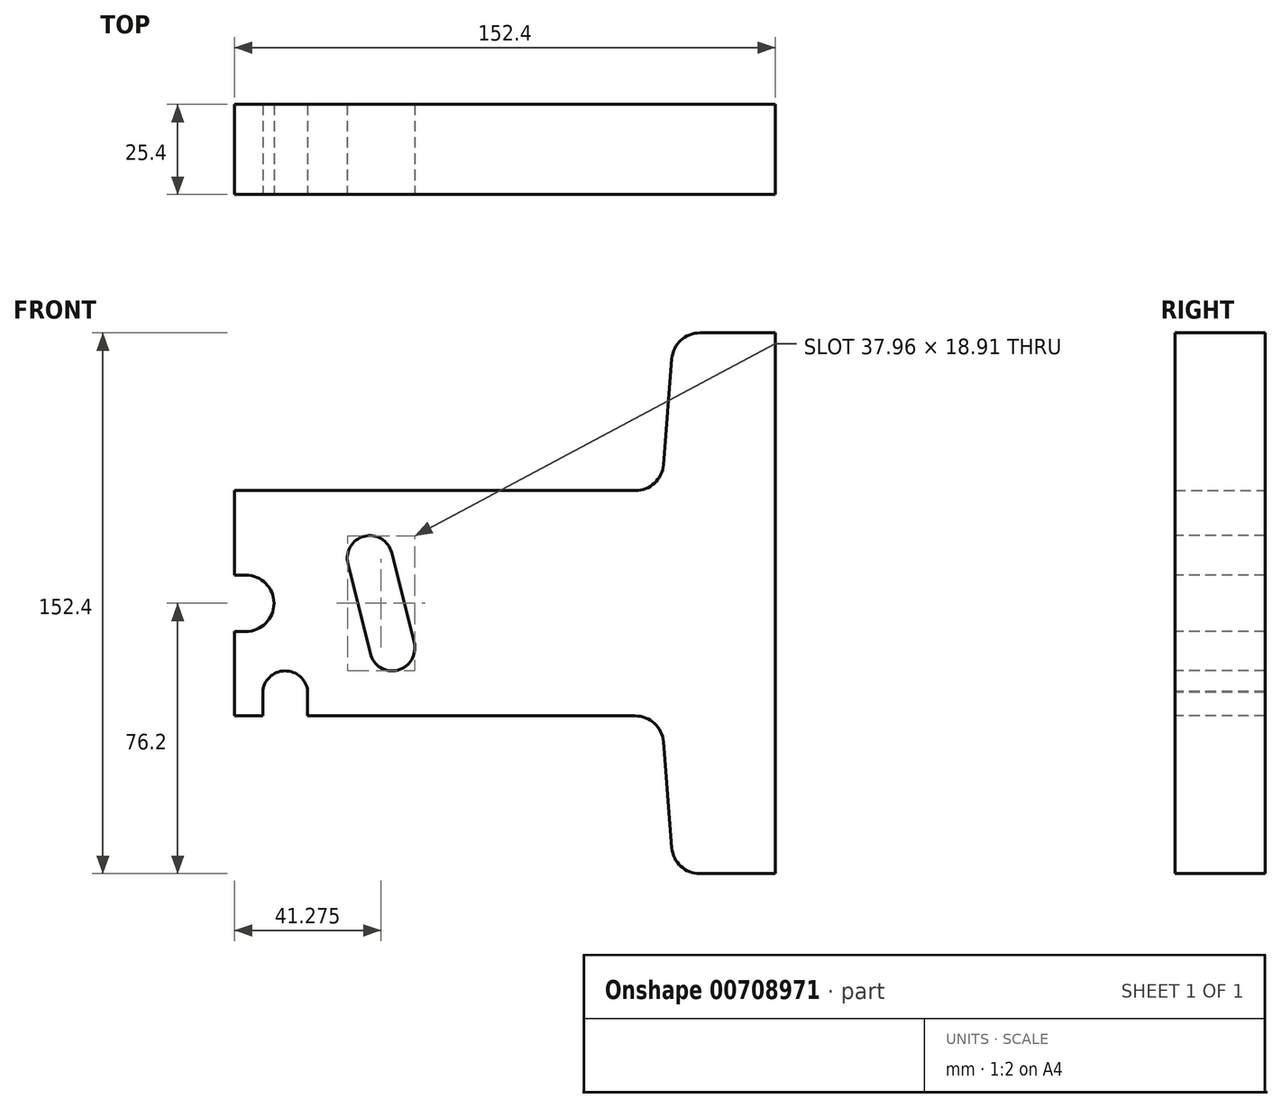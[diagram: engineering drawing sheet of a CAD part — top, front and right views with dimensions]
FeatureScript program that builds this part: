
annotation { "Feature Type Name" : "Feature", "Feature Type Description" : "" }
export const myFeature = defineFeature(function(context is Context, id is Id, definition is map)
    precondition{}
    {
        {
            var Q0;
            Q0=qCreatedBy(makeId("Front.planeOp"),FACE);
            var sketch = newSketch(context, id + "F0", { "sketchPlane" : qUnion([Q0])});
            skLineSegment(sketch, "E0", {"start": v(76.2, 0) * mm, "end": v(76.2, -76.2) * mm});
            skLineSegment(sketch, "E1", {"start": v(76.2, -76.2) * mm, "end": v(54.95, -76.2) * mm});
            skLineSegment(sketch, "E2", {"start": v(-76.2, 0) * mm, "end": v(-76.2, -31.75) * mm});
            skLineSegment(sketch, "E3", {"start": v(-76.2, -31.75) * mm, "end": v(36.73, -31.75) * mm});
            skLineSegment(sketch, "E4", {"start": v(47.04, -68.9) * mm, "end": v(44.65, -39.05) * mm});
            skLineSegment(sketch, "E5.MirrorCS", {"start": v(-76.2, 0) * mm, "end": v(-76.2, 31.75) * mm});
            skLineSegment(sketch, "E6.MirrorCS", {"start": v(-76.2, 31.75) * mm, "end": v(36.73, 31.75) * mm});
            skLineSegment(sketch, "E7.MirrorCS", {"start": v(47.04, 68.9) * mm, "end": v(44.65, 39.05) * mm});
            skLineSegment(sketch, "E8.MirrorCS", {"start": v(76.2, 76.2) * mm, "end": v(54.95, 76.2) * mm});
            skLineSegment(sketch, "E9.MirrorCS", {"start": v(76.2, 0) * mm, "end": v(76.2, 76.2) * mm});
            skPoint(sketch, "E10.visualSharp", {"position": v(44.06, 31.75) * mm});
            skArc(sketch, "E10.filletArc", {"start": v(36.73, 31.75) * mm, "mid": v(42.12, 33.85) * mm, "end": v(44.65, 39.05) * mm});
            skPoint(sketch, "E11.visualSharp", {"position": v(44.06, -31.75) * mm});
            skArc(sketch, "E11.filletArc", {"start": v(44.65, -39.05) * mm, "mid": v(42.12, -33.85) * mm, "end": v(36.73, -31.75) * mm});
            skPoint(sketch, "E12.visualSharp", {"position": v(47.63, 76.2) * mm});
            skArc(sketch, "E12.filletArc", {"start": v(54.95, 76.2) * mm, "mid": v(49.57, 74.1) * mm, "end": v(47.04, 68.9) * mm});
            skPoint(sketch, "E13.visualSharp", {"position": v(47.63, -76.2) * mm});
            skArc(sketch, "E13.filletArc", {"start": v(47.04, -68.9) * mm, "mid": v(49.57, -74.1) * mm, "end": v(54.95, -76.2) * mm});
            skSolve(sketch);
        }
        {
            var Q0;
            Q0=makeQuery(id+"F0.imprint","IMPRINT",FACE,{"disambiguationData":[TD([[makeQuery(id+"F0.imprint","IMPRINT",EDGE,{"derivedFrom":sQuery(id+"F0.wireOp",EDGE,"E0")}),-1.0]])]});
            extrude(context, id + "F1", {"entities" : qUnion([Q0]), "depth" : 25.4 * mm, "offsetDistance" : 25.4 * mm, "symmetric" : true});
        }
        {
            var Q0;
            Q0=makeQuery(id+"F1.opExtrude","CAP_FACE",FACE,{"disambiguationData":[OSD([sQuery(id+"F0.wireOp",EDGE,"E0"),sQuery(id+"F0.wireOp",EDGE,"E1"),sQuery(id+"F0.wireOp",EDGE,"E2"),sQuery(id+"F0.wireOp",EDGE,"E3"),sQuery(id+"F0.wireOp",EDGE,"E4"),sQuery(id+"F0.wireOp",EDGE,"E5.MirrorCS"),sQuery(id+"F0.wireOp",EDGE,"E6.MirrorCS"),sQuery(id+"F0.wireOp",EDGE,"E7.MirrorCS"),sQuery(id+"F0.wireOp",EDGE,"E8.MirrorCS"),sQuery(id+"F0.wireOp",EDGE,"E9.MirrorCS")])],"isStart":false});
            var sketch = newSketch(context, id + "F2", { "sketchPlane" : qUnion([Q0])});
            skLineSegment(sketch, "E14", {"start": v(-73.03, 7.94) * mm, "end": v(-76.2, 7.94) * mm});
            skLineSegment(sketch, "E15", {"start": v(-73.03, -7.94) * mm, "end": v(-76.2, -7.94) * mm});
            skLineSegment(sketch, "E16", {"start": v(-65.09, 0) * mm, "end": v(-65.09, 0) * mm});
            skPoint(sketch, "E17.visualSharp", {"position": v(-65.09, 7.94) * mm});
            skArc(sketch, "E17.filletArc", {"start": v(-65.09, 0) * mm, "mid": v(-67.41, 5.61) * mm, "end": v(-73.03, 7.94) * mm});
            skPoint(sketch, "E18.visualSharp", {"position": v(-65.09, -7.94) * mm});
            skArc(sketch, "E18.filletArc", {"start": v(-73.03, -7.94) * mm, "mid": v(-67.41, -5.61) * mm, "end": v(-65.09, 0) * mm});
            skSolve(sketch);
        }
        {
            var Q0;
            {var subQ0=sQuery(id+"F2.wireOp",EDGE,"E14");Q0=makeQuery(id+"F2.imprint","IMPRINT",FACE,{"disambiguationData":[TD([[makeQuery(id+"F2.imprint","IMPRINT",EDGE,{"derivedFrom":subQ0}),1.0]])]});}
            extrude(context, id + "F3", {"entities" : qUnion([Q0]), "operationType" : NewBodyOperationType.REMOVE, "endBound" : BoundingType.THROUGH_ALL, "oppositeDirection" : true, "depth" : 25.4 * mm, "offsetDistance" : 25.4 * mm});
        }
        {
            var Q0;
            Q0=makeQuery(id+"F1.opExtrude","CAP_FACE",FACE,{"disambiguationData":[OSD([sQuery(id+"F0.wireOp",EDGE,"E0"),sQuery(id+"F0.wireOp",EDGE,"E1"),sQuery(id+"F0.wireOp",EDGE,"E2"),sQuery(id+"F0.wireOp",EDGE,"E3"),sQuery(id+"F0.wireOp",EDGE,"E4"),sQuery(id+"F0.wireOp",EDGE,"E5.MirrorCS"),sQuery(id+"F0.wireOp",EDGE,"E6.MirrorCS"),sQuery(id+"F0.wireOp",EDGE,"E7.MirrorCS"),sQuery(id+"F0.wireOp",EDGE,"E8.MirrorCS"),sQuery(id+"F0.wireOp",EDGE,"E9.MirrorCS")])],"isStart":false});
            var sketch = newSketch(context, id + "F4", { "sketchPlane" : qUnion([Q0])});
            skCircle(sketch, "E19", {"center": v(-38.1, 12.7) * mm, "radius": 6.35 * mm});
            skCircle(sketch, "E20", {"center": v(-31.75, -12.7) * mm, "radius": 6.35 * mm});
            skLineSegment(sketch, "E21", {"start": v(-31.75, -31.75) * mm, "end": v(-31.75, -12.7) * mm, "construction": true});
            skLineSegment(sketch, "E22", {"start": v(-31.75, -12.7) * mm, "end": v(-76.2, -12.7) * mm, "construction": true});
            skArc(sketch, "E23", {"start": v(-55.59, -24.84) * mm, "mid": v(-62.04, -19.05) * mm, "end": v(-68.25, -25.1) * mm});
            skLineSegment(sketch, "E24", {"start": v(-68.25, -25.1) * mm, "end": v(-68.25, -31.75) * mm});
            skLineSegment(sketch, "E25", {"start": v(-55.59, -24.84) * mm, "end": v(-55.59, -31.75) * mm});
            skLineSegment(sketch, "E26", {"start": v(-38.1, 12.7) * mm, "end": v(-76.2, 12.7) * mm, "construction": true});
            skPoint(sketch, "E26.endSnap0", {"position": v(-76.2, 19.84) * mm});
            skLineSegment(sketch, "E27", {"start": v(-38.1, 12.7) * mm, "end": v(-38.1, 31.75) * mm, "construction": true});
            skLineSegment(sketch, "E28", {"start": v(-44.26, 11.16) * mm, "end": v(-37.91, -14.24) * mm});
            skLineSegment(sketch, "E29", {"start": v(-31.94, 14.24) * mm, "end": v(-25.59, -11.16) * mm});
            skSolve(sketch);
        }
        {
            var Q0;
            {var subQ0=sQuery(id+"F4.wireOp",EDGE,"E20");var subQ1=makeQuery(id+"F4.imprint","INTERSECT",VERTEX,{"derivedFrom":[subQ0,sQuery(id+"F4.wireOp",EDGE,"E28")]});Q0=makeQuery(id+"F4.imprint","IMPRINT",FACE,{"disambiguationData":[TD([[makeQuery(id+"F4.imprint","IMPRINT",EDGE,{"disambiguationData":[TD([[subQ1,1.0]])],"derivedFrom":subQ0}),1.0]])]});}
            var Q1;
            {var subQ0=sQuery(id+"F4.wireOp",EDGE,"E28");Q1=makeQuery(id+"F4.imprint","IMPRINT",FACE,{"disambiguationData":[TD([[makeQuery(id+"F4.imprint","IMPRINT",EDGE,{"derivedFrom":subQ0}),1.0]])]});}
            var Q2;
            {var subQ0=sQuery(id+"F4.wireOp",EDGE,"E19");var subQ1=makeQuery(id+"F4.imprint","INTERSECT",VERTEX,{"derivedFrom":[subQ0,sQuery(id+"F4.wireOp",EDGE,"E28")]});Q2=makeQuery(id+"F4.imprint","IMPRINT",FACE,{"disambiguationData":[TD([[makeQuery(id+"F4.imprint","IMPRINT",EDGE,{"disambiguationData":[TD([[subQ1,1.0]])],"derivedFrom":subQ0}),1.0]])]});}
            var Q3;
            Q3=makeQuery(id+"F4.imprint","IMPRINT",FACE,{"disambiguationData":[TD([[makeQuery(id+"F4.imprint","IMPRINT",EDGE,{"derivedFrom":sQuery(id+"F4.wireOp",EDGE,"E23")}),1.0]])]});
            extrude(context, id + "F5", {"entities" : qUnion([Q0, Q1, Q2, Q3]), "operationType" : NewBodyOperationType.REMOVE, "oppositeDirection" : true, "depth" : 25.4 * mm, "offsetDistance" : 25.4 * mm});
        }
    });
